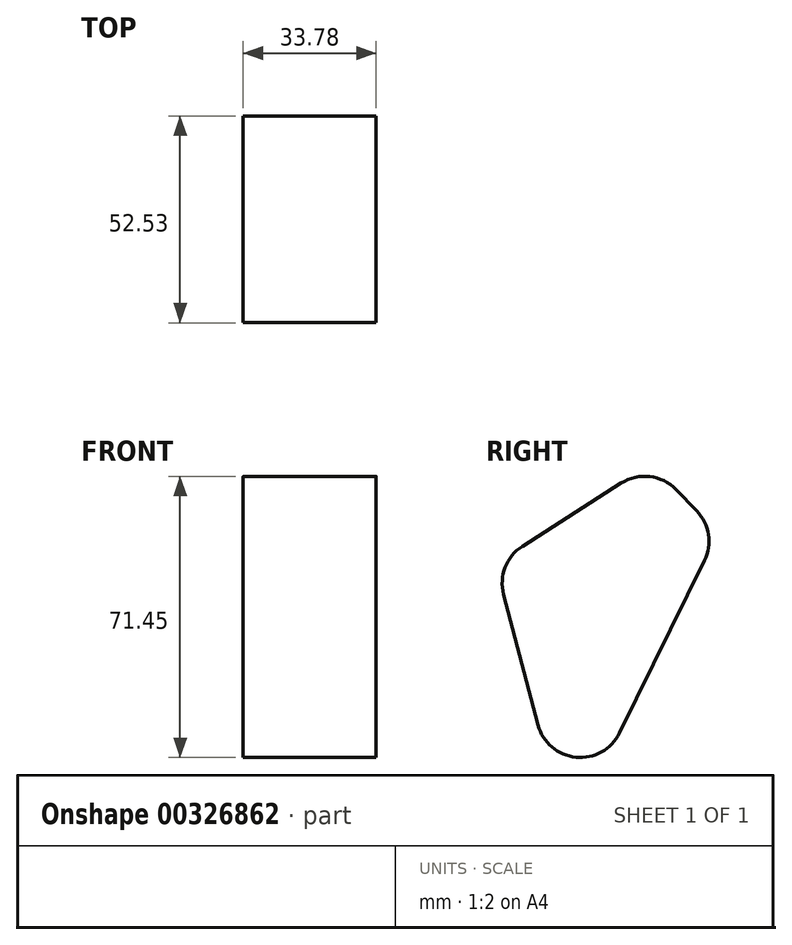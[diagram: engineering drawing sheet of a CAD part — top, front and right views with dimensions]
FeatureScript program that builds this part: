
annotation { "Feature Type Name" : "Feature", "Feature Type Description" : "" }
export const myFeature = defineFeature(function(context is Context, id is Id, definition is map)
    precondition{}
    {
        {
            var Q0;
            Q0=qCreatedBy(makeId("Right.planeOp"),FACE);
            var sketch = newSketch(context, id + "F0", { "sketchPlane" : qUnion([Q0])});
            skLineSegment(sketch, "E0", {"start": v(-64.35, 30.73) * mm, "end": v(-24.78, 56.07) * mm});
            skLineSegment(sketch, "E1", {"start": v(-24.78, 56.07) * mm, "end": v(-7.82, 38.47) * mm});
            skLineSegment(sketch, "E2", {"start": v(-7.82, 38.47) * mm, "end": v(-45.98, -38.94) * mm});
            skLineSegment(sketch, "E3", {"start": v(-45.98, -38.94) * mm, "end": v(-64.35, 30.73) * mm});
            skSolve(sketch);
        }
        {
            var Q0;
            Q0=makeQuery(id+"F0.imprint","IMPRINT",FACE,{"disambiguationData":[TD([[makeQuery(id+"F0.imprint","IMPRINT",EDGE,{"derivedFrom":sQuery(id+"F0.wireOp",EDGE,"E0")}),-1.0]])]});
            extrude(context, id + "F1", {"entities" : qUnion([Q0]), "oppositeDirection" : true, "depth" : 33.78 * mm});
        }
        {
            var Q0;
            Q0=makeQuery(id+"F1.opExtrude","SWEPT_EDGE",EDGE,{"disambiguationData":[OSD([sQuery(id+"F0.wireOp",EDGE,"E0"),sQuery(id+"F0.wireOp",EDGE,"E1")])]});
            var Q1;
            Q1=makeQuery(id+"F1.opExtrude","SWEPT_EDGE",EDGE,{"disambiguationData":[OSD([sQuery(id+"F0.wireOp",EDGE,"E1"),sQuery(id+"F0.wireOp",EDGE,"E2")])]});
            var Q2;
            Q2=makeQuery(id+"F1.opExtrude","SWEPT_EDGE",EDGE,{"disambiguationData":[OSD([sQuery(id+"F0.wireOp",EDGE,"E0"),sQuery(id+"F0.wireOp",EDGE,"E3")])]});
            var Q3;
            Q3=makeQuery(id+"F1.opExtrude","SWEPT_EDGE",EDGE,{"disambiguationData":[OSD([sQuery(id+"F0.wireOp",EDGE,"E2"),sQuery(id+"F0.wireOp",EDGE,"E3")])]});
            fillet(context, id + "F2", {"entities" : qUnion([Q0, Q1, Q2, Q3]), "radius" : 11.1 * mm, "tangentPropagation" : true, "allowEdgeOverflow" : false});
        }
    });
